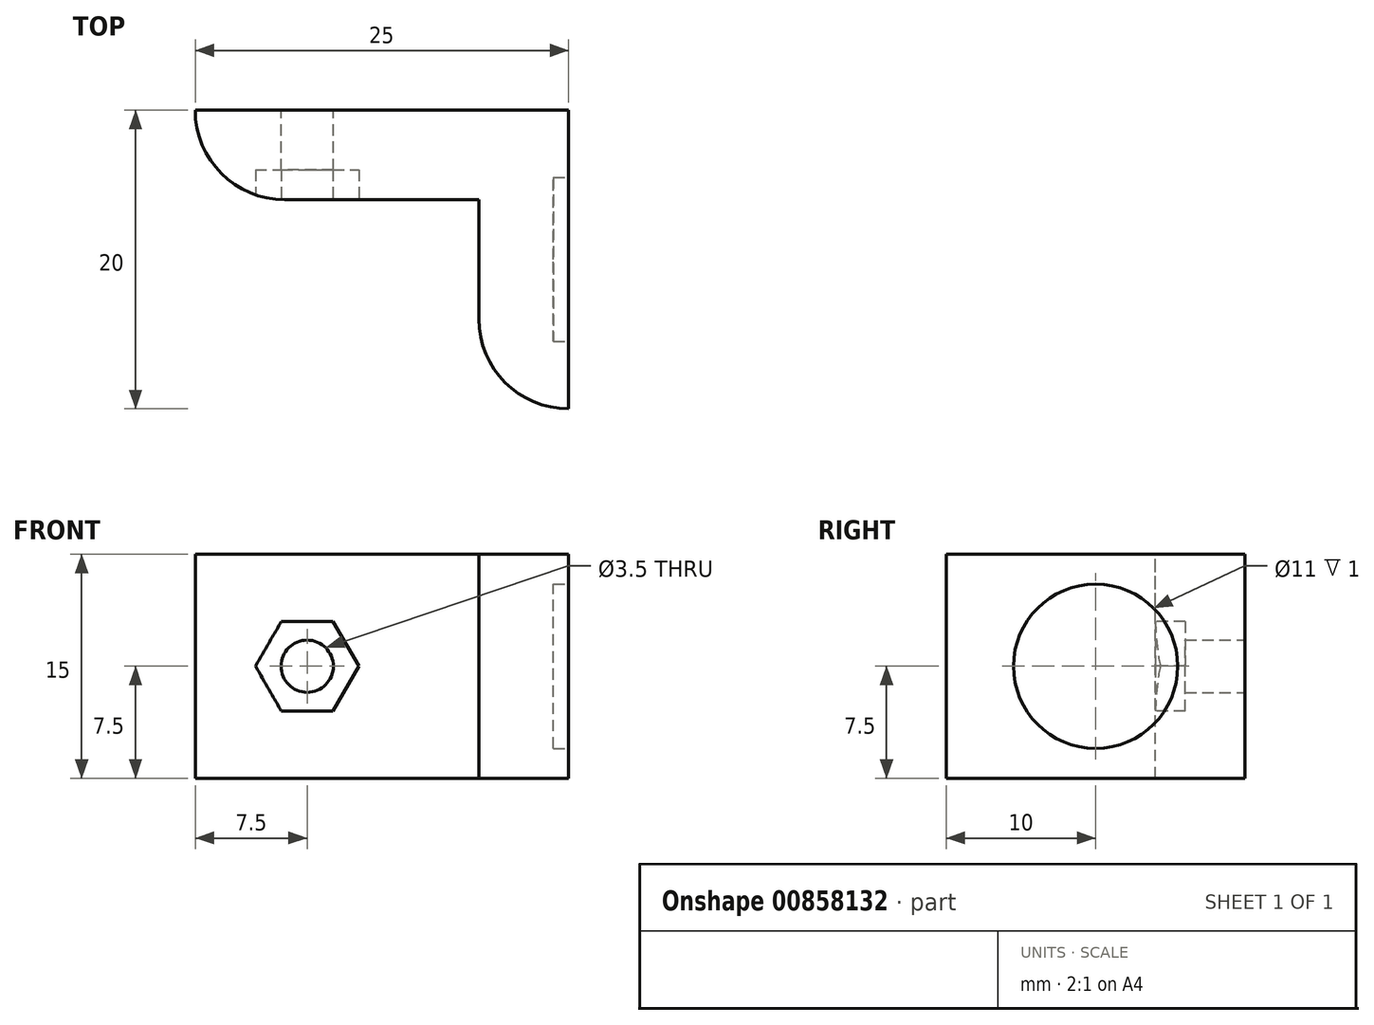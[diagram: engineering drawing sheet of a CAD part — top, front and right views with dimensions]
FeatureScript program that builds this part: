
annotation { "Feature Type Name" : "Feature", "Feature Type Description" : "" }
export const myFeature = defineFeature(function(context is Context, id is Id, definition is map)
    precondition{}
    {
        {
            assignVariable(context, id + "F0", {"name" : "thickness", "anyValue" : 6});
        }
        {
            assignVariable(context, id + "F1", {"name" : "magnet_hole_depth", "anyValue" : 1 * mm});
        }
        {
            assignVariable(context, id + "F2", {"name" : "nut_height", "anyValue" : 2 * mm});
        }
        {
            var Q0;
            Q0=qCreatedBy(makeId("Front.planeOp"),FACE);
            var sketch = newSketch(context, id + "F3", { "sketchPlane" : qUnion([Q0])});
            skLineSegment(sketch, "E0.bottom", {"start": v(0, 0) * mm, "end": v(25, 0) * mm});
            skLineSegment(sketch, "E0.top", {"start": v(0, 15) * mm, "end": v(25, 15) * mm});
            skLineSegment(sketch, "E0.left", {"start": v(0, 0) * mm, "end": v(0, 15) * mm});
            skLineSegment(sketch, "E0.right", {"start": v(25, 0) * mm, "end": v(25, 15) * mm});
            skLineSegment(sketch, "E1", {"start": v(25, 7.5) * mm, "end": v(7.5, 7.5) * mm, "construction": true});
            skLineSegment(sketch, "E2", {"start": v(7.5, 7.5) * mm, "end": v(7.5, 15) * mm, "construction": true});
            skCircle(sketch, "E3", {"center": v(7.5, 7.5) * mm, "radius": 1.75 * mm});
            skSolve(sketch);
        }
        {
            var Q0;
            Q0=makeQuery(id+"F3.imprint","IMPRINT",FACE,{"disambiguationData":[TD([[makeQuery(id+"F3.imprint","IMPRINT",EDGE,{"derivedFrom":sQuery(id+"F3.wireOp",EDGE,"E0.bottom")}),1.0]])]});
            extrude(context, id + "F4", {"entities" : qUnion([Q0]), "depth" : (getVariable(context, 'thickness')) * mm, "offsetDistance" : 25 * mm});
        }
        {
            var Q0;
            Q0=makeQuery(id+"F4.opExtrude","SWEPT_FACE",FACE,{"disambiguationData":[OSD([sQuery(id+"F3.wireOp",EDGE,"E0.right")])]});
            var sketch = newSketch(context, id + "F5", { "sketchPlane" : qUnion([Q0])});
            skLineSegment(sketch, "E4.bottom", {"start": v(-6, 15) * mm, "end": v(-20, 15) * mm});
            skLineSegment(sketch, "E4.top", {"start": v(-6, 0) * mm, "end": v(-20, 0) * mm});
            skLineSegment(sketch, "E4.left", {"start": v(-6, 15) * mm, "end": v(-6, 0) * mm});
            skLineSegment(sketch, "E4.right", {"start": v(-20, 15) * mm, "end": v(-20, 0) * mm});
            skSolve(sketch);
        }
        {
            var Q0;
            Q0=makeQuery(id+"F5.imprint","IMPRINT",FACE,{"disambiguationData":[TD([[makeQuery(id+"F5.imprint","IMPRINT",EDGE,{"derivedFrom":sQuery(id+"F5.wireOp",EDGE,"E4.bottom")}),1.0]])]});
            extrude(context, id + "F6", {"entities" : qUnion([Q0]), "operationType" : NewBodyOperationType.ADD, "oppositeDirection" : true, "depth" : (getVariable(context, 'thickness')) * mm, "offsetDistance" : 25 * mm});
        }
        {
            var Q0;
            Q0=makeQuery(id+"F6.boolean.opBoolean","MERGE",FACE,{"derivedFrom":[makeQuery(id+"F4.opExtrude","SWEPT_FACE",FACE,{"disambiguationData":[OSD([sQuery(id+"F3.wireOp",EDGE,"E0.right")])]}),makeQuery(id+"F6.opExtrude","CAP_FACE",FACE,{"disambiguationData":[OSD([sQuery(id+"F5.wireOp",EDGE,"E4.bottom"),sQuery(id+"F5.wireOp",EDGE,"E4.top"),sQuery(id+"F5.wireOp",EDGE,"E4.left"),sQuery(id+"F5.wireOp",EDGE,"E4.right")])],"isStart":true})]});
            var sketch = newSketch(context, id + "F7", { "sketchPlane" : qUnion([Q0])});
            skLineSegment(sketch, "E5", {"start": v(-20, 15) * mm, "end": v(0, 0) * mm, "construction": true});
            skCircle(sketch, "E6", {"center": v(-10, 7.5) * mm, "radius": 5.5 * mm});
            skSolve(sketch);
        }
        {
            var Q0;
            Q0=makeQuery(id+"F7.imprint","IMPRINT",FACE,{"disambiguationData":[TD([[makeQuery(id+"F7.imprint","IMPRINT",EDGE,{"derivedFrom":sQuery(id+"F7.wireOp",EDGE,"E6")}),1.0]])]});
            var Q1;
            Q1=sQuery(id+"F7.wireOp",EDGE,"E6");
            extrude(context, id + "F8", {"entities" : qUnion([Q0]), "operationType" : NewBodyOperationType.REMOVE, "surfaceEntities" : qUnion([Q1]), "oppositeDirection" : true, "depth" : getVariable(context, 'magnet_hole_depth'), "offsetDistance" : 25 * mm});
        }
        {
            var Q0;
            Q0=makeQuery(id+"F4.opExtrude","CAP_FACE",FACE,{"disambiguationData":[OSD([sQuery(id+"F3.wireOp",EDGE,"E0.bottom"),sQuery(id+"F3.wireOp",EDGE,"E0.top"),sQuery(id+"F3.wireOp",EDGE,"E0.left"),sQuery(id+"F3.wireOp",EDGE,"E0.right"),sQuery(id+"F3.wireOp",EDGE,"E3")])],"isStart":false});
            var sketch = newSketch(context, id + "F9", { "sketchPlane" : qUnion([Q0])});
            skCircle(sketch, "E7.cCircle", {"center": v(7.5, 7.5) * mm, "radius": 3 * mm, "construction": true});
            skLineSegment(sketch, "E7.0", {"start": v(9.23, 10.5) * mm, "end": v(10.96, 7.5) * mm});
            skLineSegment(sketch, "E7.1", {"start": v(10.96, 7.5) * mm, "end": v(9.23, 4.5) * mm});
            skLineSegment(sketch, "E7.2", {"start": v(9.23, 4.5) * mm, "end": v(5.77, 4.5) * mm});
            skLineSegment(sketch, "E7.3", {"start": v(5.77, 4.5) * mm, "end": v(4.04, 7.5) * mm});
            skLineSegment(sketch, "E7.4", {"start": v(4.04, 7.5) * mm, "end": v(5.77, 10.5) * mm});
            skLineSegment(sketch, "E7.5", {"start": v(5.77, 10.5) * mm, "end": v(9.23, 10.5) * mm});
            skPoint(sketch, "E7.0.midPoint", {"position": v(10.1, 9) * mm});
            skSolve(sketch);
        }
        {
            var Q0;
            Q0=makeQuery(id+"F9.imprint","IMPRINT",FACE,{"disambiguationData":[TD([[makeQuery(id+"F9.imprint","IMPRINT",EDGE,{"derivedFrom":sQuery(id+"F9.wireOp",EDGE,"E7.0")}),-1.0]])]});
            extrude(context, id + "F10", {"entities" : qUnion([Q0]), "operationType" : NewBodyOperationType.REMOVE, "oppositeDirection" : true, "depth" : getVariable(context, 'nut_height'), "offsetDistance" : 25 * mm});
        }
        {
            var Q0;
            Q0=makeQuery(id+"F6.opExtrude","CAP_EDGE",EDGE,{"disambiguationData":[OSD([sQuery(id+"F5.wireOp",EDGE,"E4.left")])],"isStart":false});
            var Q1;
            Q1=makeQuery(id+"F4.opExtrude","CAP_EDGE",EDGE,{"disambiguationData":[OSD([sQuery(id+"F3.wireOp",EDGE,"E0.left")])],"isStart":false});
            var Q2;
            Q2=makeQuery(id+"F6.opExtrude","CAP_EDGE",EDGE,{"disambiguationData":[OSD([sQuery(id+"F5.wireOp",EDGE,"E4.right")])],"isStart":false});
            fillet(context, id + "F11", {"entities" : qUnion([Q0, Q1, Q2]), "radius" : 6 * mm, "tangentPropagation" : true, "allowEdgeOverflow" : false});
        }
    });
